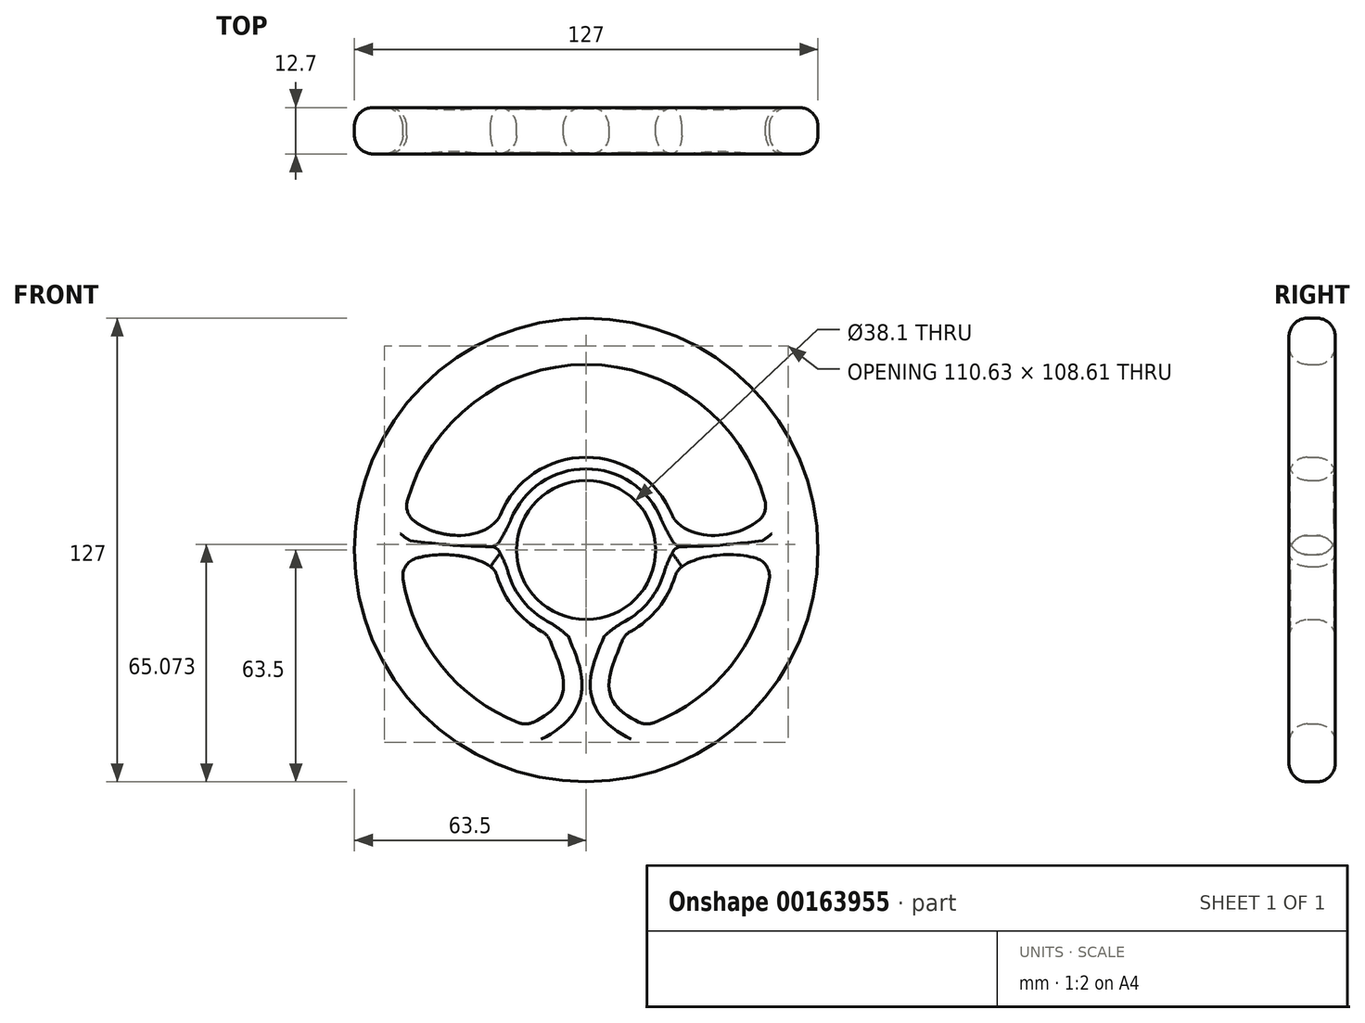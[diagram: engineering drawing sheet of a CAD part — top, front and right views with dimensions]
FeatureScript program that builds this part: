
annotation { "Feature Type Name" : "Feature", "Feature Type Description" : "" }
export const myFeature = defineFeature(function(context is Context, id is Id, definition is map)
    precondition{}
    {
        {
            var Q0;
            Q0=qCreatedBy(makeId("Front.planeOp"),FACE);
            var sketch = newSketch(context, id + "F0", { "sketchPlane" : qUnion([Q0])});
            skCircle(sketch, "E0", {"center": v(0, 0) * mm, "radius": 25.4 * mm});
            skCircle(sketch, "E1", {"center": v(0, 0) * mm, "radius": 50.8 * mm});
            skFitSpline(sketch, "E2", {"points": [v(-23.78, 8.93) * mm, v(-49.55, 11.2) * mm], "startDerivative": vector(-19.04, -26.8) * mm, "endDerivative": vector(-6.47, 19.62) * mm});
            skFitSpline(sketch, "E3", {"points": [v(-24.72, -5.84) * mm, v(-50.6, -4.55) * mm], "startDerivative": vector(-16.22, 17.52) * mm, "endDerivative": vector(-12.18, -13.66) * mm});
            skLineSegment(sketch, "E4", {"start": v(-23.78, 8.93) * mm, "end": v(23.78, 8.93) * mm});
            skLineSegment(sketch, "E5", {"start": v(-49.55, 11.2) * mm, "end": v(49.55, 11.2) * mm});
            skLineSegment(sketch, "E6", {"start": v(-24.72, -5.84) * mm, "end": v(24.72, -5.84) * mm});
            skLineSegment(sketch, "E7", {"start": v(-50.6, -4.55) * mm, "end": v(50.6, -4.55) * mm});
            skFitSpline(sketch, "E8.MirrorCS", {"points": [v(23.78, 8.93) * mm, v(49.55, 11.2) * mm], "startDerivative": vector(19.04, -26.8) * mm, "endDerivative": vector(6.47, 19.62) * mm});
            skFitSpline(sketch, "E9.MirrorCS", {"points": [v(24.72, -5.84) * mm, v(50.6, -4.55) * mm], "startDerivative": vector(16.22, 17.52) * mm, "endDerivative": vector(12.18, -13.66) * mm});
            skFitSpline(sketch, "E10", {"points": [v(-10.5, -23.13) * mm, v(-16.5, -48.05) * mm], "startDerivative": vector(8.63, -26.28) * mm, "endDerivative": vector(-49.48, -19.72) * mm});
            skFitSpline(sketch, "E11.MirrorCS", {"points": [v(10.5, -23.13) * mm, v(16.5, -48.05) * mm], "startDerivative": vector(-8.63, -26.28) * mm, "endDerivative": vector(49.48, -19.72) * mm});
            skCircle(sketch, "E12", {"center": v(0, 0) * mm, "radius": 19.05 * mm});
            skCircle(sketch, "E13", {"center": v(0, 0) * mm, "radius": 63.5 * mm});
            skSolve(sketch);
        }
        {
            var Q0;
            {var subQ1=sQuery(id+"F0.wireOp",EDGE,"E0");var subQ3=sQuery(id+"F0.wireOp",EDGE,"E7");var subQ4=makeQuery(id+"F0.imprint","INTERSECT",VERTEX,{"disambiguationData":[OD(0.0)],"derivedFrom":[subQ1,subQ3]});Q0=makeQuery(id+"F0.imprint","IMPRINT",FACE,{"disambiguationData":[TD([[makeQuery(id+"F0.imprint","IMPRINT",EDGE,{"disambiguationData":[TD([[subQ4,-1.0]])],"derivedFrom":subQ3}),1.0]])]});}
            var Q1;
            {var subQ0=sQuery(id+"F0.wireOp",EDGE,"E5");var subQ1=sQuery(id+"F0.wireOp",EDGE,"E0");var subQ2=makeQuery(id+"F0.imprint","INTERSECT",VERTEX,{"disambiguationData":[OD(0.0)],"derivedFrom":[subQ1,subQ0]});Q1=makeQuery(id+"F0.imprint","IMPRINT",FACE,{"disambiguationData":[TD([[makeQuery(id+"F0.imprint","IMPRINT",EDGE,{"disambiguationData":[TD([[subQ2,-1.0]])],"derivedFrom":subQ1}),1.0]])]});}
            var Q2;
            {var subQ1=sQuery(id+"F0.wireOp",EDGE,"E0");var subQ3=sQuery(id+"F0.wireOp",EDGE,"E7");var subQ4=makeQuery(id+"F0.imprint","INTERSECT",VERTEX,{"disambiguationData":[OD(1.0)],"derivedFrom":[subQ1,subQ3]});Q2=makeQuery(id+"F0.imprint","IMPRINT",FACE,{"disambiguationData":[TD([[makeQuery(id+"F0.imprint","IMPRINT",EDGE,{"disambiguationData":[TD([[subQ4,1.0]])],"derivedFrom":subQ3}),1.0]])]});}
            var Q3;
            {var subQ0=sQuery(id+"F0.wireOp",EDGE,"E8.MirrorCS");Q3=makeQuery(id+"F0.imprint","IMPRINT",FACE,{"disambiguationData":[TD([[makeQuery(id+"F0.imprint","IMPRINT",EDGE,{"derivedFrom":subQ0}),-1.0]])]});}
            var Q4;
            {var subQ0=sQuery(id+"F0.wireOp",EDGE,"E10");Q4=makeQuery(id+"F0.imprint","IMPRINT",FACE,{"disambiguationData":[TD([[makeQuery(id+"F0.imprint","IMPRINT",EDGE,{"derivedFrom":subQ0}),1.0]])]});}
            var Q5;
            {var subQ0=sQuery(id+"F0.wireOp",EDGE,"E2");Q5=makeQuery(id+"F0.imprint","IMPRINT",FACE,{"disambiguationData":[TD([[makeQuery(id+"F0.imprint","IMPRINT",EDGE,{"derivedFrom":subQ0}),1.0]])]});}
            var Q6;
            Q6=makeQuery(id+"F0.imprint","IMPRINT",FACE,{"disambiguationData":[TD([[makeQuery(id+"F0.imprint","IMPRINT",EDGE,{"derivedFrom":sQuery(id+"F0.wireOp",EDGE,"E13")}),1.0]])]});
            var Q7;
            {var subQ1=sQuery(id+"F0.wireOp",EDGE,"E0");var subQ3=sQuery(id+"F0.wireOp",EDGE,"E5");var subQ4=makeQuery(id+"F0.imprint","INTERSECT",VERTEX,{"disambiguationData":[OD(0.0)],"derivedFrom":[subQ1,subQ3]});Q7=makeQuery(id+"F0.imprint","IMPRINT",FACE,{"disambiguationData":[TD([[makeQuery(id+"F0.imprint","IMPRINT",EDGE,{"disambiguationData":[TD([[subQ4,1.0]])],"derivedFrom":subQ3}),-1.0]])]});}
            var Q8;
            {var subQ1=sQuery(id+"F0.wireOp",EDGE,"E0");var subQ3=sQuery(id+"F0.wireOp",EDGE,"E7");var subQ4=makeQuery(id+"F0.imprint","INTERSECT",VERTEX,{"disambiguationData":[OD(1.0)],"derivedFrom":[subQ1,subQ3]});Q8=makeQuery(id+"F0.imprint","IMPRINT",FACE,{"disambiguationData":[TD([[makeQuery(id+"F0.imprint","IMPRINT",EDGE,{"disambiguationData":[TD([[subQ4,1.0]])],"derivedFrom":subQ3}),-1.0]])]});}
            var Q9;
            {var subQ1=sQuery(id+"F0.wireOp",EDGE,"E0");var subQ7=makeQuery(id+"F0.imprint","INTERSECT",VERTEX,{"derivedFrom":[subQ1,sQuery(id+"F0.wireOp",EDGE,"E10")]});Q9=makeQuery(id+"F0.imprint","IMPRINT",FACE,{"disambiguationData":[TD([[makeQuery(id+"F0.imprint","IMPRINT",EDGE,{"disambiguationData":[TD([[subQ7,-1.0]])],"derivedFrom":subQ1}),1.0]])]});}
            var Q10;
            {var subQ1=sQuery(id+"F0.wireOp",EDGE,"E0");var subQ3=sQuery(id+"F0.wireOp",EDGE,"E7");var subQ4=makeQuery(id+"F0.imprint","INTERSECT",VERTEX,{"disambiguationData":[OD(0.0)],"derivedFrom":[subQ1,subQ3]});Q10=makeQuery(id+"F0.imprint","IMPRINT",FACE,{"disambiguationData":[TD([[makeQuery(id+"F0.imprint","IMPRINT",EDGE,{"disambiguationData":[TD([[subQ4,-1.0]])],"derivedFrom":subQ3}),-1.0]])]});}
            var Q11;
            {var subQ1=sQuery(id+"F0.wireOp",EDGE,"E0");var subQ3=sQuery(id+"F0.wireOp",EDGE,"E5");var subQ4=makeQuery(id+"F0.imprint","INTERSECT",VERTEX,{"disambiguationData":[OD(1.0)],"derivedFrom":[subQ1,subQ3]});Q11=makeQuery(id+"F0.imprint","IMPRINT",FACE,{"disambiguationData":[TD([[makeQuery(id+"F0.imprint","IMPRINT",EDGE,{"disambiguationData":[TD([[subQ4,-1.0]])],"derivedFrom":subQ3}),-1.0]])]});}
            extrude(context, id + "F1", {"entities" : qUnion([Q0, Q1, Q2, Q3, Q4, Q5, Q6, Q7, Q8, Q9, Q10, Q11]), "depth" : 12.7 * mm});
        }
        {
            var Q0;
            Q0=makeQuery(id+"F1.opExtrude","SWEPT_EDGE",EDGE,{"disambiguationData":[OSD([sQuery(id+"F0.wireOp",EDGE,"E1"),sQuery(id+"F0.wireOp",EDGE,"E10")])]});
            var Q1;
            Q1=makeQuery(id+"F1.opExtrude","SWEPT_EDGE",EDGE,{"disambiguationData":[OSD([sQuery(id+"F0.wireOp",EDGE,"E1"),sQuery(id+"F0.wireOp",EDGE,"E11.MirrorCS")])]});
            var Q2;
            {var subQ0=sQuery(id+"F0.wireOp",EDGE,"E7");var subQ1=sQuery(id+"F0.wireOp",EDGE,"E0");Q2=makeQuery(id+"F1.opExtrude","SWEPT_EDGE",EDGE,{"disambiguationData":[OSD([subQ1,subQ0]),TDD([makeQuery(id+"F0.imprint","INTERSECT",VERTEX,{"disambiguationData":[OD(1.0)],"derivedFrom":[subQ1,subQ0]})])]});}
            var Q3;
            Q3=makeQuery(id+"F1.opExtrude","SWEPT_EDGE",EDGE,{"disambiguationData":[OSD([sQuery(id+"F0.wireOp",EDGE,"E0"),sQuery(id+"F0.wireOp",EDGE,"E11.MirrorCS")])]});
            var Q4;
            Q4=makeQuery(id+"F1.opExtrude","SWEPT_EDGE",EDGE,{"disambiguationData":[OSD([sQuery(id+"F0.wireOp",EDGE,"E1"),sQuery(id+"F0.wireOp",EDGE,"E7"),sQuery(id+"F0.wireOp",EDGE,"E9.MirrorCS")])]});
            var Q5;
            Q5=makeQuery(id+"F1.opExtrude","SWEPT_EDGE",EDGE,{"disambiguationData":[OSD([sQuery(id+"F0.wireOp",EDGE,"E1"),sQuery(id+"F0.wireOp",EDGE,"E5"),sQuery(id+"F0.wireOp",EDGE,"E8.MirrorCS")])]});
            var Q6;
            Q6=makeQuery(id+"F1.opExtrude","SWEPT_EDGE",EDGE,{"disambiguationData":[OSD([sQuery(id+"F0.wireOp",EDGE,"E0"),sQuery(id+"F0.wireOp",EDGE,"E4"),sQuery(id+"F0.wireOp",EDGE,"E8.MirrorCS")])]});
            var Q7;
            Q7=makeQuery(id+"F1.opExtrude","SWEPT_EDGE",EDGE,{"disambiguationData":[OSD([sQuery(id+"F0.wireOp",EDGE,"E0"),sQuery(id+"F0.wireOp",EDGE,"E2"),sQuery(id+"F0.wireOp",EDGE,"E4")])]});
            var Q8;
            Q8=makeQuery(id+"F1.opExtrude","SWEPT_EDGE",EDGE,{"disambiguationData":[OSD([sQuery(id+"F0.wireOp",EDGE,"E1"),sQuery(id+"F0.wireOp",EDGE,"E2"),sQuery(id+"F0.wireOp",EDGE,"E5")])]});
            var Q9;
            {var subQ0=sQuery(id+"F0.wireOp",EDGE,"E7");var subQ1=sQuery(id+"F0.wireOp",EDGE,"E0");Q9=makeQuery(id+"F1.opExtrude","SWEPT_EDGE",EDGE,{"disambiguationData":[OSD([subQ1,subQ0]),TDD([makeQuery(id+"F0.imprint","INTERSECT",VERTEX,{"disambiguationData":[OD(0.0)],"derivedFrom":[subQ1,subQ0]})])]});}
            var Q10;
            Q10=makeQuery(id+"F1.opExtrude","SWEPT_EDGE",EDGE,{"disambiguationData":[OSD([sQuery(id+"F0.wireOp",EDGE,"E1"),sQuery(id+"F0.wireOp",EDGE,"E3"),sQuery(id+"F0.wireOp",EDGE,"E7")])]});
            var Q11;
            Q11=makeQuery(id+"F1.opExtrude","SWEPT_EDGE",EDGE,{"disambiguationData":[OSD([sQuery(id+"F0.wireOp",EDGE,"E0"),sQuery(id+"F0.wireOp",EDGE,"E10")])]});
            fillet(context, id + "F2", {"entities" : qUnion([Q0, Q1, Q2, Q3, Q4, Q5, Q6, Q7, Q8, Q9, Q10, Q11]), "radius" : 5.08 * mm, "tangentPropagation" : true, "allowEdgeOverflow" : false});
        }
        {
            var Q0;
            Q0=makeQuery(id+"F1.opExtrude","CAP_EDGE",EDGE,{"disambiguationData":[OSD([sQuery(id+"F0.wireOp",EDGE,"E13")])],"isStart":true});
            var Q1;
            Q1=makeQuery(id+"F1.opExtrude","CAP_EDGE",EDGE,{"disambiguationData":[OSD([sQuery(id+"F0.wireOp",EDGE,"E13")])],"isStart":false});
            var Q2;
            Q2=makeQuery(id+"F1.opExtrude","CAP_FACE",FACE,{"disambiguationData":[OSD([sQuery(id+"F0.wireOp",EDGE,"E0"),sQuery(id+"F0.wireOp",EDGE,"E1"),sQuery(id+"F0.wireOp",EDGE,"E2"),sQuery(id+"F0.wireOp",EDGE,"E3"),sQuery(id+"F0.wireOp",EDGE,"E7"),sQuery(id+"F0.wireOp",EDGE,"E8.MirrorCS"),sQuery(id+"F0.wireOp",EDGE,"E9.MirrorCS"),sQuery(id+"F0.wireOp",EDGE,"E10"),sQuery(id+"F0.wireOp",EDGE,"E11.MirrorCS"),sQuery(id+"F0.wireOp",EDGE,"E12"),sQuery(id+"F0.wireOp",EDGE,"E13")])],"isStart":false});
            var Q3;
            Q3=makeQuery(id+"F1.opExtrude","CAP_FACE",FACE,{"disambiguationData":[OSD([sQuery(id+"F0.wireOp",EDGE,"E0"),sQuery(id+"F0.wireOp",EDGE,"E1"),sQuery(id+"F0.wireOp",EDGE,"E2"),sQuery(id+"F0.wireOp",EDGE,"E3"),sQuery(id+"F0.wireOp",EDGE,"E7"),sQuery(id+"F0.wireOp",EDGE,"E8.MirrorCS"),sQuery(id+"F0.wireOp",EDGE,"E9.MirrorCS"),sQuery(id+"F0.wireOp",EDGE,"E10"),sQuery(id+"F0.wireOp",EDGE,"E11.MirrorCS"),sQuery(id+"F0.wireOp",EDGE,"E12"),sQuery(id+"F0.wireOp",EDGE,"E13")])],"isStart":true});
            fillet(context, id + "F3", {"entities" : qUnion([Q0, Q1, Q2, Q3]), "radius" : 5.08 * mm, "tangentPropagation" : true, "allowEdgeOverflow" : false});
        }
    });
